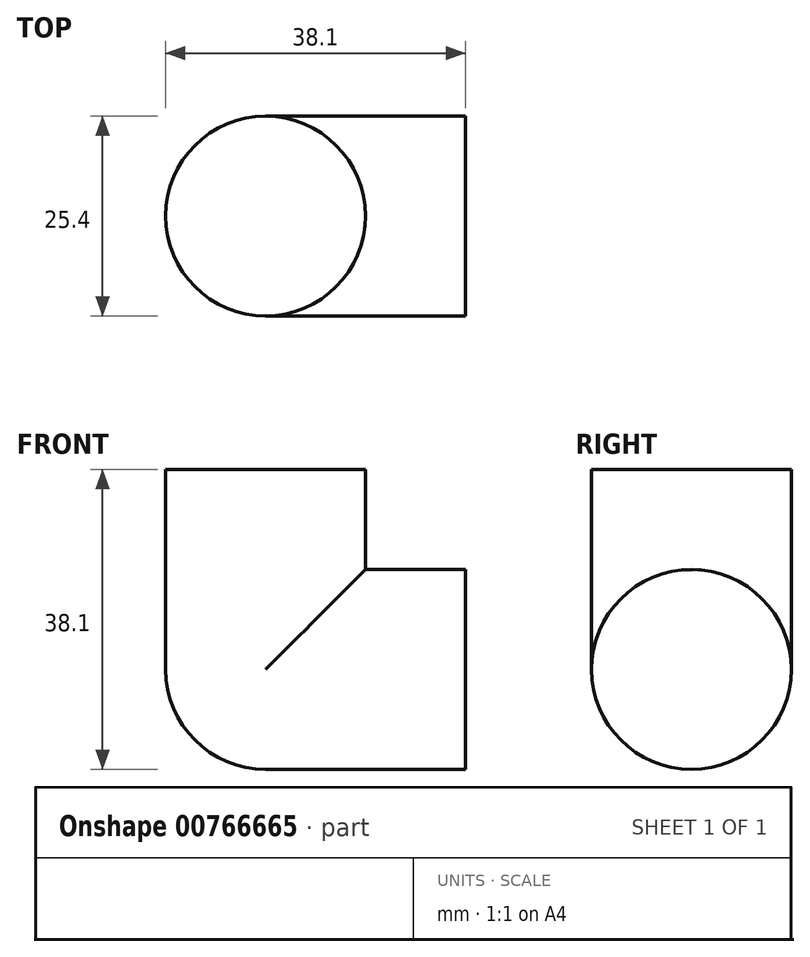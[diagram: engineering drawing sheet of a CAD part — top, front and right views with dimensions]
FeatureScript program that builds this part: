
annotation { "Feature Type Name" : "Feature", "Feature Type Description" : "" }
export const myFeature = defineFeature(function(context is Context, id is Id, definition is map)
    precondition{}
    {
        {
            var Q0;
            Q0=qCreatedBy(makeId("Front.planeOp"),FACE);
            var sketch = newSketch(context, id + "F0", { "sketchPlane" : qUnion([Q0])});
            skCircle(sketch, "E0", {"center": v(0, 0) * mm, "radius": 12.7 * mm});
            skLineSegment(sketch, "E1", {"start": v(0, 21.35) * mm, "end": v(0, -24.01) * mm});
            skSolve(sketch);
        }
        {
            var Q0;
            {var subQ0=sQuery(id+"F0.wireOp",EDGE,"E1");var subQ1=sQuery(id+"F0.wireOp",EDGE,"E0");var subQ2=makeQuery(id+"F0.imprint","INTERSECT",VERTEX,{"disambiguationData":[OD(0.0)],"derivedFrom":[subQ1,subQ0]});Q0=makeQuery(id+"F0.imprint","IMPRINT",FACE,{"disambiguationData":[TD([[makeQuery(id+"F0.imprint","IMPRINT",EDGE,{"disambiguationData":[TD([[subQ2,1.0]])],"derivedFrom":subQ1}),1.0]])]});}
            var Q1;
            Q1=sQuery(id+"F0.wireOp",EDGE,"E1");
            revolve(context, id + "F1", {"surfaceOperationType" : NewSurfaceOperationType.NEW, "entities" : qUnion([Q0]), "axis" : qUnion([Q1]), "revolveType" : RevolveType.FULL});
        }
        {
            var Q0;
            Q0=qCreatedBy(makeId("Right.planeOp"),FACE);
            var sketch = newSketch(context, id + "F2", { "sketchPlane" : qUnion([Q0])});
            skCircle(sketch, "E2", {"center": v(0, 0) * mm, "radius": 12.7 * mm});
            skSolve(sketch);
        }
        {
            var Q0;
            Q0 = qSketchRegion(id + "F2", true);
            extrude(context, id + "F3", {"entities" : qUnion([Q0]), "operationType" : NewBodyOperationType.ADD, "depth" : 25.4 * mm, "offsetDistance" : 25.4 * mm});
        }
        {
            var Q0;
            Q0=qCreatedBy(makeId("Top.planeOp"),FACE);
            var sketch = newSketch(context, id + "F4", { "sketchPlane" : qUnion([Q0])});
            skCircle(sketch, "E3", {"center": v(0, 0) * mm, "radius": 12.7 * mm});
            skSolve(sketch);
        }
        {
            var Q0;
            Q0=sQuery(id+"F4.wireOp",EDGE,"E3");
            extrude(context, id + "F5", {"bodyType" : ToolBodyType.SURFACE, "surfaceEntities" : qUnion([Q0]), "depth" : 25.4 * mm, "offsetDistance" : 25.4 * mm});
        }
        {
            var Q0;
            Q0=makeQuery(id+"F5.opExtrude","SWEPT_BODY",BODY,{"disambiguationData":[OSD([sQuery(id+"F4.wireOp",EDGE,"E3")])]});
            deleteBodies(context, id + "F6", {"entities" : qUnion([Q0])});
        }
        {
            var Q0;
            Q0=qCreatedBy(makeId("Top.planeOp"),FACE);
            var sketch = newSketch(context, id + "F7", { "sketchPlane" : qUnion([Q0])});
            skCircle(sketch, "E4", {"center": v(0, 0) * mm, "radius": 12.7 * mm});
            skSolve(sketch);
        }
        {
            var Q0;
            Q0 = qSketchRegion(id + "F7", true);
            extrude(context, id + "F8", {"entities" : qUnion([Q0]), "operationType" : NewBodyOperationType.ADD, "depth" : 25.4 * mm, "offsetDistance" : 25.4 * mm});
        }
    });
